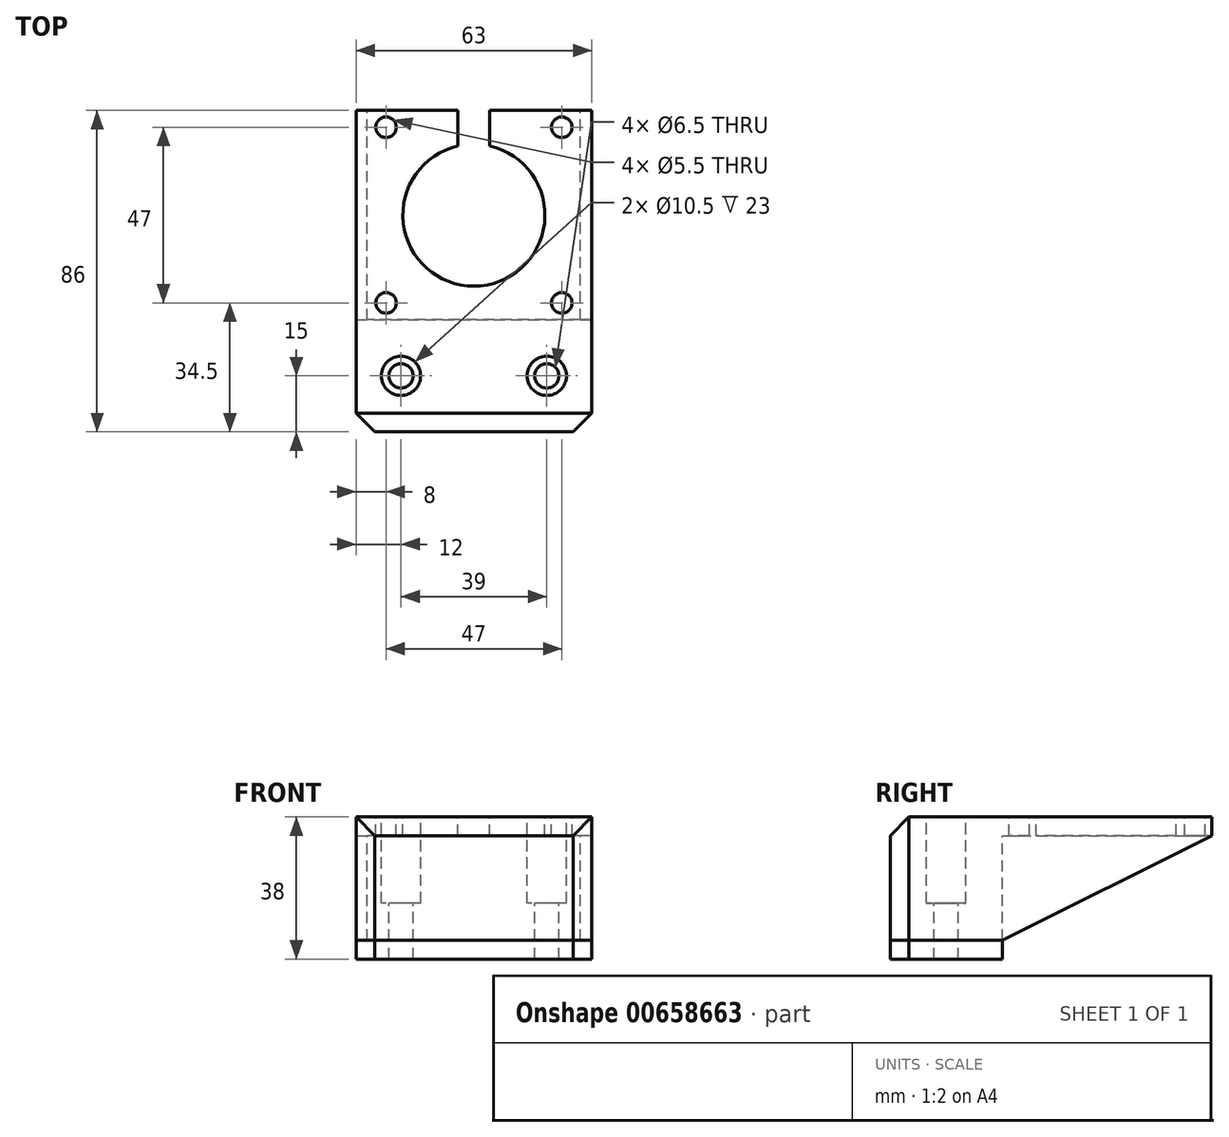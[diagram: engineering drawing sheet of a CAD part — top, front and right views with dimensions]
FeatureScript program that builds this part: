
annotation { "Feature Type Name" : "Feature", "Feature Type Description" : "" }
export const myFeature = defineFeature(function(context is Context, id is Id, definition is map)
    precondition{}
    {
        {
            var Q0;
            Q0=qCreatedBy(makeId("Top.planeOp"),FACE);
            var sketch = newSketch(context, id + "F0", { "sketchPlane" : qUnion([Q0])});
            skLineSegment(sketch, "E0.rect.bottom", {"start": v(28.5, -28) * mm, "end": v(-28.5, -28) * mm});
            skLineSegment(sketch, "E0.rect.top", {"start": v(28.5, 28) * mm, "end": v(-28.5, 28) * mm});
            skLineSegment(sketch, "E0.rect.left", {"start": v(28.5, -28) * mm, "end": v(28.5, 28) * mm});
            skLineSegment(sketch, "E0.rect.right", {"start": v(-28.5, -28) * mm, "end": v(-28.5, 28) * mm});
            skPoint(sketch, "E0.rect.middle", {"position": v(0, 0) * mm});
            skSolve(sketch);
        }
        {
            var Q0;
            Q0=makeQuery(id+"F0.imprint","IMPRINT",FACE,{"disambiguationData":[TD([[makeQuery(id+"F0.imprint","IMPRINT",EDGE,{"derivedFrom":sQuery(id+"F0.wireOp",EDGE,"E0.rect.bottom")}),-1.0]])]});
            extrude(context, id + "F1", {"entities" : qUnion([Q0]), "depth" : 5 * mm});
        }
        {
            var Q0;
            Q0=makeQuery(id+"F1.opExtrude","CAP_FACE",FACE,{"disambiguationData":[OSD([sQuery(id+"F0.wireOp",EDGE,"E0.rect.bottom"),sQuery(id+"F0.wireOp",EDGE,"E0.rect.top"),sQuery(id+"F0.wireOp",EDGE,"E0.rect.left"),sQuery(id+"F0.wireOp",EDGE,"E0.rect.right")])],"isStart":false});
            var sketch = newSketch(context, id + "F2", { "sketchPlane" : qUnion([Q0])});
            skArc(sketch, "E1", {"start": v(-4.25, 18.52) * mm, "mid": v(0, -19) * mm, "end": v(4.25, 18.52) * mm});
            skLineSegment(sketch, "E2.bottom", {"start": v(-4.25, 28) * mm, "end": v(4.25, 28) * mm});
            skLineSegment(sketch, "E2.left", {"start": v(-4.25, 28) * mm, "end": v(-4.25, 18.52) * mm});
            skLineSegment(sketch, "E2.right", {"start": v(4.25, 28) * mm, "end": v(4.25, 18.52) * mm});
            skCircle(sketch, "E3", {"center": v(-23.5, 23.5) * mm, "radius": 2.75 * mm});
            skCircle(sketch, "E4.0.1.0", {"center": v(-23.5, -23.5) * mm, "radius": 2.75 * mm});
            skCircle(sketch, "E4.1.0.0", {"center": v(23.5, 23.5) * mm, "radius": 2.75 * mm});
            skCircle(sketch, "E4.1.1.0", {"center": v(23.5, -23.5) * mm, "radius": 2.75 * mm});
            skLineSegment(sketch, "E4.direction1", {"start": v(-23.5, 23.5) * mm, "end": v(23.5, 23.5) * mm, "construction": true});
            skLineSegment(sketch, "E4.direction2", {"start": v(-23.5, 23.5) * mm, "end": v(-23.5, -23.5) * mm, "construction": true});
            skSolve(sketch);
        }
        {
            var Q0;
            Q0=makeQuery(id+"F2.imprint","IMPRINT",FACE,{"disambiguationData":[TD([[makeQuery(id+"F2.imprint","IMPRINT",EDGE,{"derivedFrom":sQuery(id+"F2.wireOp",EDGE,"E4.0.1.0")}),1.0]])]});
            var Q1;
            Q1=makeQuery(id+"F2.imprint","IMPRINT",FACE,{"disambiguationData":[TD([[makeQuery(id+"F2.imprint","IMPRINT",EDGE,{"derivedFrom":sQuery(id+"F2.wireOp",EDGE,"E4.1.1.0")}),1.0]])]});
            var Q2;
            Q2=makeQuery(id+"F2.imprint","IMPRINT",FACE,{"disambiguationData":[TD([[makeQuery(id+"F2.imprint","IMPRINT",EDGE,{"derivedFrom":sQuery(id+"F2.wireOp",EDGE,"E4.1.0.0")}),1.0]])]});
            var Q3;
            Q3=makeQuery(id+"F2.imprint","IMPRINT",FACE,{"disambiguationData":[TD([[makeQuery(id+"F2.imprint","IMPRINT",EDGE,{"derivedFrom":sQuery(id+"F2.wireOp",EDGE,"E3")}),1.0]])]});
            var Q4;
            Q4=makeQuery(id+"F2.imprint","IMPRINT",FACE,{"disambiguationData":[TD([[makeQuery(id+"F2.imprint","IMPRINT",EDGE,{"derivedFrom":sQuery(id+"F2.wireOp",EDGE,"E1")}),1.0]])]});
            extrude(context, id + "F3", {"entities" : qUnion([Q0, Q1, Q2, Q3, Q4]), "operationType" : NewBodyOperationType.REMOVE, "oppositeDirection" : true, "depth" : 25 * mm});
        }
        {
            var Q0;
            Q0=makeQuery(id+"F1.opExtrude","CAP_FACE",FACE,{"disambiguationData":[OSD([sQuery(id+"F0.wireOp",EDGE,"E0.rect.bottom"),sQuery(id+"F0.wireOp",EDGE,"E0.rect.top"),sQuery(id+"F0.wireOp",EDGE,"E0.rect.left"),sQuery(id+"F0.wireOp",EDGE,"E0.rect.right")])],"isStart":false});
            var sketch = newSketch(context, id + "F4", { "sketchPlane" : qUnion([Q0])});
            skLineSegment(sketch, "E5.bottom", {"start": v(-28.5, -28) * mm, "end": v(28.5, -28) * mm});
            skLineSegment(sketch, "E5.top", {"start": v(-28.5, -58) * mm, "end": v(28.5, -58) * mm});
            skLineSegment(sketch, "E5.left", {"start": v(-28.5, -28) * mm, "end": v(-28.5, -58) * mm});
            skLineSegment(sketch, "E5.right", {"start": v(28.5, -28) * mm, "end": v(28.5, -58) * mm});
            skSolve(sketch);
        }
        {
            var Q0;
            Q0=makeQuery(id+"F4.imprint","IMPRINT",FACE,{"disambiguationData":[TD([[makeQuery(id+"F4.imprint","IMPRINT",EDGE,{"derivedFrom":sQuery(id+"F4.wireOp",EDGE,"E5.bottom")}),1.0]])]});
            extrude(context, id + "F5", {"entities" : qUnion([Q0]), "operationType" : NewBodyOperationType.ADD, "oppositeDirection" : true, "depth" : 33 * mm});
        }
        {
            var Q0;
            Q0=makeQuery(id+"F5.boolean.opBoolean","MERGE",FACE,{"derivedFrom":[makeQuery(id+"F1.opExtrude","CAP_FACE",FACE,{"disambiguationData":[OSD([sQuery(id+"F0.wireOp",EDGE,"E0.rect.bottom"),sQuery(id+"F0.wireOp",EDGE,"E0.rect.top"),sQuery(id+"F0.wireOp",EDGE,"E0.rect.left"),sQuery(id+"F0.wireOp",EDGE,"E0.rect.right")])],"isStart":false}),makeQuery(id+"F5.opExtrude","CAP_FACE",FACE,{"disambiguationData":[OSD([sQuery(id+"F4.wireOp",EDGE,"E5.bottom"),sQuery(id+"F4.wireOp",EDGE,"E5.top"),sQuery(id+"F4.wireOp",EDGE,"E5.left"),sQuery(id+"F4.wireOp",EDGE,"E5.right")])],"isStart":true})]});
            var sketch = newSketch(context, id + "F6", { "sketchPlane" : qUnion([Q0])});
            skCircle(sketch, "E6", {"center": v(-19.5, -43) * mm, "radius": 5.25 * mm});
            skCircle(sketch, "E7", {"center": v(19.5, -43) * mm, "radius": 5.25 * mm});
            skSolve(sketch);
        }
        {
            var Q0;
            Q0=makeQuery(id+"F6.imprint","IMPRINT",FACE,{"disambiguationData":[TD([[makeQuery(id+"F6.imprint","IMPRINT",EDGE,{"derivedFrom":sQuery(id+"F6.wireOp",EDGE,"E6")}),1.0]])]});
            var Q1;
            Q1=makeQuery(id+"F6.imprint","IMPRINT",FACE,{"disambiguationData":[TD([[makeQuery(id+"F6.imprint","IMPRINT",EDGE,{"derivedFrom":sQuery(id+"F6.wireOp",EDGE,"E7")}),1.0]])]});
            extrude(context, id + "F7", {"entities" : qUnion([Q0, Q1]), "operationType" : NewBodyOperationType.REMOVE, "oppositeDirection" : true, "depth" : 23 * mm});
        }
        {
            var Q0;
            Q0=makeQuery(id+"F5.boolean.opBoolean","MERGE",FACE,{"derivedFrom":[makeQuery(id+"F1.opExtrude","CAP_FACE",FACE,{"disambiguationData":[OSD([sQuery(id+"F0.wireOp",EDGE,"E0.rect.bottom"),sQuery(id+"F0.wireOp",EDGE,"E0.rect.top"),sQuery(id+"F0.wireOp",EDGE,"E0.rect.left"),sQuery(id+"F0.wireOp",EDGE,"E0.rect.right")])],"isStart":false}),makeQuery(id+"F5.opExtrude","CAP_FACE",FACE,{"disambiguationData":[OSD([sQuery(id+"F4.wireOp",EDGE,"E5.bottom"),sQuery(id+"F4.wireOp",EDGE,"E5.top"),sQuery(id+"F4.wireOp",EDGE,"E5.left"),sQuery(id+"F4.wireOp",EDGE,"E5.right")])],"isStart":true})]});
            var sketch = newSketch(context, id + "F8", { "sketchPlane" : qUnion([Q0])});
            skCircle(sketch, "E8.0", {"center": v(-19.5, -43) * mm, "radius": 5.25 * mm});
            skCircle(sketch, "E9.0", {"center": v(19.5, -43) * mm, "radius": 5.25 * mm});
            skCircle(sketch, "E10", {"center": v(-19.5, -43) * mm, "radius": 3.25 * mm});
            skCircle(sketch, "E11", {"center": v(19.5, -43) * mm, "radius": 3.25 * mm});
            skSolve(sketch);
        }
        {
            var Q0;
            Q0=makeQuery(id+"F8.imprint","IMPRINT",FACE,{"disambiguationData":[TD([[makeQuery(id+"F8.imprint","IMPRINT",EDGE,{"derivedFrom":sQuery(id+"F8.wireOp",EDGE,"E10")}),1.0]])]});
            var Q1;
            Q1=makeQuery(id+"F8.imprint","IMPRINT",FACE,{"disambiguationData":[TD([[makeQuery(id+"F8.imprint","IMPRINT",EDGE,{"derivedFrom":sQuery(id+"F8.wireOp",EDGE,"E11")}),1.0]])]});
            extrude(context, id + "F9", {"entities" : qUnion([Q0, Q1]), "operationType" : NewBodyOperationType.REMOVE, "endBound" : BoundingType.THROUGH_ALL, "oppositeDirection" : true, "depth" : 25 * mm});
        }
        {
            var Q0;
            Q0=makeQuery(id+"F5.boolean.opBoolean","MERGE",FACE,{"derivedFrom":[makeQuery(id+"F1.opExtrude","SWEPT_FACE",FACE,{"disambiguationData":[OSD([sQuery(id+"F0.wireOp",EDGE,"E0.rect.left")])]}),makeQuery(id+"F5.opExtrude","SWEPT_FACE",FACE,{"disambiguationData":[OSD([sQuery(id+"F4.wireOp",EDGE,"E5.right")])]})]});
            var sketch = newSketch(context, id + "F10", { "sketchPlane" : qUnion([Q0])});
            skLineSegment(sketch, "E12.0.0", {"start": v(-28, 0) * mm, "end": v(28, 0) * mm});
            skLineSegment(sketch, "E12.0.1", {"start": v(28, 0) * mm, "end": v(28, 5) * mm});
            skLineSegment(sketch, "E12.0.2", {"start": v(28, 5) * mm, "end": v(-58, 5) * mm});
            skLineSegment(sketch, "E12.0.3", {"start": v(-58, 5) * mm, "end": v(-58, -28) * mm});
            skLineSegment(sketch, "E12.0.4", {"start": v(-58, -28) * mm, "end": v(-28, -28) * mm});
            skLineSegment(sketch, "E12.0.5", {"start": v(-28, -28) * mm, "end": v(-28, 0) * mm});
            skLineSegment(sketch, "E13", {"start": v(-28, -28) * mm, "end": v(28, 0) * mm});
            skSolve(sketch);
        }
        {
            var Q0;
            Q0=makeQuery(id+"F10.imprint","IMPRINT",FACE,{"disambiguationData":[TD([[makeQuery(id+"F10.imprint","IMPRINT",EDGE,{"derivedFrom":sQuery(id+"F10.wireOp",EDGE,"E12.0.0")}),1.0]])]});
            var Q1;
            Q1=makeQuery(id+"F10.imprint","IMPRINT",FACE,{"disambiguationData":[TD([[makeQuery(id+"F10.imprint","IMPRINT",EDGE,{"derivedFrom":sQuery(id+"F10.wireOp",EDGE,"E12.0.0")}),-1.0]])]});
            extrude(context, id + "F11", {"entities" : qUnion([Q0, Q1]), "operationType" : NewBodyOperationType.ADD, "depth" : 3 * mm});
        }
        {
            var Q0;
            Q0=makeQuery(id+"F5.boolean.opBoolean","MERGE",FACE,{"derivedFrom":[makeQuery(id+"F1.opExtrude","SWEPT_FACE",FACE,{"disambiguationData":[OSD([sQuery(id+"F0.wireOp",EDGE,"E0.rect.right")])]}),makeQuery(id+"F5.opExtrude","SWEPT_FACE",FACE,{"disambiguationData":[OSD([sQuery(id+"F4.wireOp",EDGE,"E5.left")])]})]});
            var sketch = newSketch(context, id + "F12", { "sketchPlane" : qUnion([Q0])});
            skLineSegment(sketch, "E14.0.0", {"start": v(-28, 0) * mm, "end": v(28, 0) * mm});
            skLineSegment(sketch, "E14.0.1", {"start": v(28, 0) * mm, "end": v(28, -28) * mm});
            skLineSegment(sketch, "E14.0.2", {"start": v(28, -28) * mm, "end": v(58, -28) * mm});
            skLineSegment(sketch, "E14.0.3", {"start": v(58, -28) * mm, "end": v(58, 5) * mm});
            skLineSegment(sketch, "E14.0.4", {"start": v(58, 5) * mm, "end": v(-28, 5) * mm});
            skLineSegment(sketch, "E14.0.5", {"start": v(-28, 5) * mm, "end": v(-28, 0) * mm});
            skLineSegment(sketch, "E15", {"start": v(-28, 0) * mm, "end": v(28, -28) * mm});
            skSolve(sketch);
        }
        {
            var Q0;
            Q0=makeQuery(id+"F12.imprint","IMPRINT",FACE,{"disambiguationData":[TD([[makeQuery(id+"F12.imprint","IMPRINT",EDGE,{"derivedFrom":sQuery(id+"F12.wireOp",EDGE,"E14.0.0")}),-1.0]])]});
            var Q1;
            Q1=makeQuery(id+"F12.imprint","IMPRINT",FACE,{"disambiguationData":[TD([[makeQuery(id+"F12.imprint","IMPRINT",EDGE,{"derivedFrom":sQuery(id+"F12.wireOp",EDGE,"E14.0.0")}),1.0]])]});
            extrude(context, id + "F13", {"entities" : qUnion([Q0, Q1]), "operationType" : NewBodyOperationType.ADD, "depth" : 3 * mm});
        }
        {
            var Q0;
            Q0=makeQuery(id+"F11.opExtrude","CAP_EDGE",EDGE,{"disambiguationData":[OSD([sQuery(id+"F10.wireOp",EDGE,"E12.0.3")])],"isStart":false});
            var Q1;
            Q1=makeQuery(id+"F13.opExtrude","CAP_EDGE",EDGE,{"disambiguationData":[OSD([sQuery(id+"F12.wireOp",EDGE,"E14.0.3")])],"isStart":false});
            var Q2;
            Q2=makeQuery(id+"F13.boolean.opBoolean","MERGE",EDGE,{"derivedFrom":[makeQuery(id+"F11.boolean.opBoolean","MERGE",EDGE,{"derivedFrom":[makeQuery(id+"F5.opExtrude","CAP_EDGE",EDGE,{"disambiguationData":[OSD([sQuery(id+"F4.wireOp",EDGE,"E5.top")])],"isStart":true}),makeQuery(id+"F11.opExtrude","SWEPT_EDGE",EDGE,{"disambiguationData":[OSD([sQuery(id+"F10.wireOp",EDGE,"E12.0.2"),sQuery(id+"F10.wireOp",EDGE,"E12.0.3")])]})]}),makeQuery(id+"F13.opExtrude","SWEPT_EDGE",EDGE,{"disambiguationData":[OSD([sQuery(id+"F12.wireOp",EDGE,"E14.0.3"),sQuery(id+"F12.wireOp",EDGE,"E14.0.4")])]})]});
            chamfer(context, id + "F14", {"entities" : qUnion([Q0, Q1, Q2]), "width" : 5 * mm, "tangentPropagation" : true});
        }
        {
            var Q0;
            Q0=makeQuery(id+"F13.boolean.opBoolean","MERGE",FACE,{"derivedFrom":[makeQuery(id+"F11.boolean.opBoolean","MERGE",FACE,{"derivedFrom":[makeQuery(id+"F5.opExtrude","CAP_FACE",FACE,{"disambiguationData":[OSD([sQuery(id+"F4.wireOp",EDGE,"E5.bottom"),sQuery(id+"F4.wireOp",EDGE,"E5.top"),sQuery(id+"F4.wireOp",EDGE,"E5.left"),sQuery(id+"F4.wireOp",EDGE,"E5.right")])],"isStart":false}),makeQuery(id+"F11.opExtrude","SWEPT_FACE",FACE,{"disambiguationData":[OSD([sQuery(id+"F10.wireOp",EDGE,"E12.0.4")])]})]}),makeQuery(id+"F13.opExtrude","SWEPT_FACE",FACE,{"disambiguationData":[OSD([sQuery(id+"F12.wireOp",EDGE,"E14.0.2")])]})]});
            var sketch = newSketch(context, id + "F15", { "sketchPlane" : qUnion([Q0])});
            skLineSegment(sketch, "E16.0.0", {"start": v(26.5, 58) * mm, "end": v(-26.5, 58) * mm});
            skLineSegment(sketch, "E16.0.1", {"start": v(-26.5, 58) * mm, "end": v(-31.5, 53) * mm});
            skLineSegment(sketch, "E16.0.2", {"start": v(-31.5, 53) * mm, "end": v(-31.5, 28) * mm});
            skLineSegment(sketch, "E16.0.3", {"start": v(-31.5, 28) * mm, "end": v(-28.5, 28) * mm});
            skLineSegment(sketch, "E16.0.4", {"start": v(-28.5, 28) * mm, "end": v(28.5, 28) * mm});
            skLineSegment(sketch, "E16.0.5", {"start": v(28.5, 28) * mm, "end": v(31.5, 28) * mm});
            skLineSegment(sketch, "E16.0.6", {"start": v(31.5, 28) * mm, "end": v(31.5, 53) * mm});
            skLineSegment(sketch, "E16.0.7", {"start": v(31.5, 53) * mm, "end": v(26.5, 58) * mm});
            skCircle(sketch, "E17.0", {"center": v(19.5, 43) * mm, "radius": 3.25 * mm});
            skCircle(sketch, "E18.0", {"center": v(-19.5, 43) * mm, "radius": 3.25 * mm});
            skSolve(sketch);
        }
        {
            var Q0;
            Q0=makeQuery(id+"F15.imprint","IMPRINT",FACE,{"disambiguationData":[TD([[makeQuery(id+"F15.imprint","IMPRINT",EDGE,{"derivedFrom":sQuery(id+"F15.wireOp",EDGE,"E16.0.0")}),-1.0]])]});
            extrude(context, id + "F16", {"entities" : qUnion([Q0]), "depth" : 5 * mm});
        }
    });
